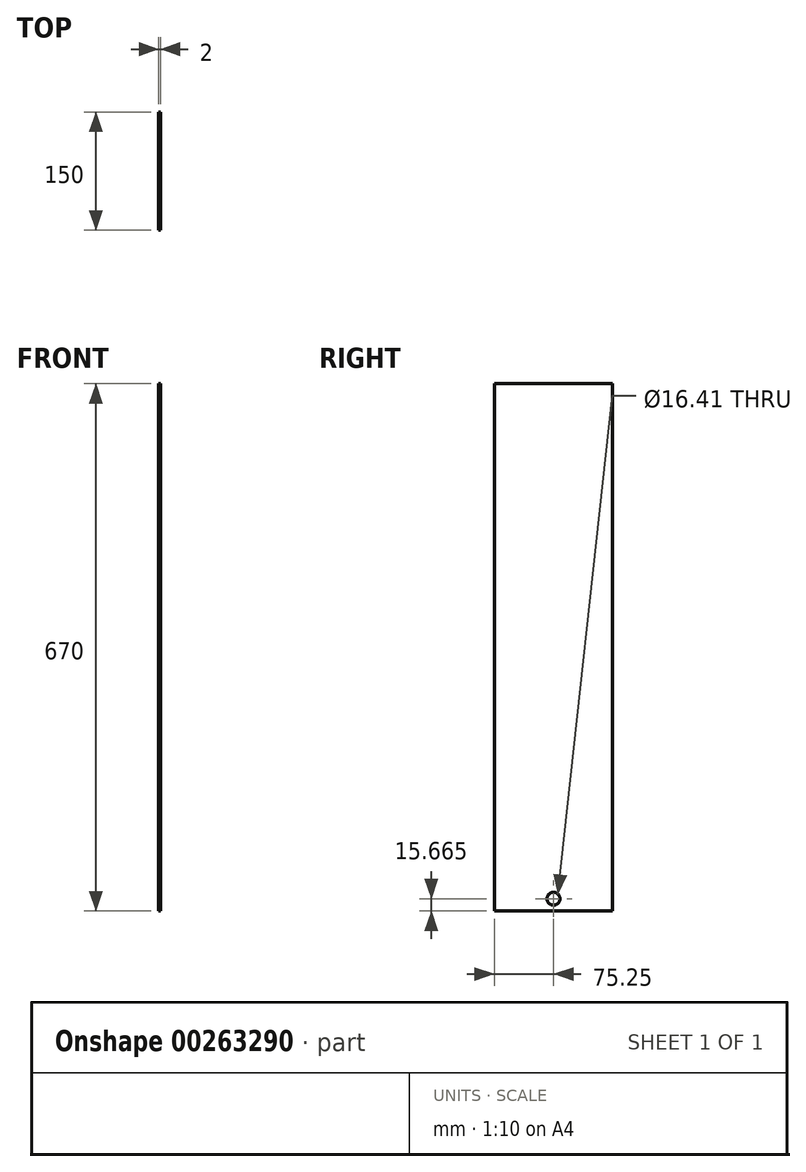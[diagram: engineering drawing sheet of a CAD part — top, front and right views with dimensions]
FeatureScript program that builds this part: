
annotation { "Feature Type Name" : "Feature", "Feature Type Description" : "" }
export const myFeature = defineFeature(function(context is Context, id is Id, definition is map)
    precondition{}
    {
        {
            var Q0;
            Q0=qCreatedBy(makeId("Right.planeOp"),FACE);
            var sketch = newSketch(context, id + "F0", { "sketchPlane" : qUnion([Q0])});
            skLineSegment(sketch, "E0.bottom", {"start": v(-80.14, -335) * mm, "end": v(69.86, -335) * mm});
            skLineSegment(sketch, "E0.top", {"start": v(-80.14, 335) * mm, "end": v(69.86, 335) * mm});
            skLineSegment(sketch, "E0.left", {"start": v(-80.14, -335) * mm, "end": v(-80.14, 335) * mm});
            skLineSegment(sketch, "E0.right", {"start": v(69.86, -335) * mm, "end": v(69.86, 335) * mm});
            skPoint(sketch, "E0.middle", {"position": v(-5.14, 0) * mm});
            skSolve(sketch);
        }
        {
            var Q0;
            Q0 = qSketchRegion(id + "F0", true);
            extrude(context, id + "F1", {"entities" : qUnion([Q0]), "depth" : 2 * mm});
        }
        {
            var Q0;
            Q0=makeQuery(id+"F1.opExtrude","CAP_FACE",FACE,{"disambiguationData":[OSD([sQuery(id+"F0.wireOp",EDGE,"E0.bottom"),sQuery(id+"F0.wireOp",EDGE,"E0.top"),sQuery(id+"F0.wireOp",EDGE,"E0.left"),sQuery(id+"F0.wireOp",EDGE,"E0.right")])],"isStart":true});
            var sketch = newSketch(context, id + "F2", { "sketchPlane" : qUnion([Q0])});
            skCircle(sketch, "E1", {"center": v(4.9, -319.33) * mm, "radius": 8.2 * mm});
            skSolve(sketch);
        }
        {
            var Q0;
            Q0 = qSketchRegion(id + "F2", true);
            extrude(context, id + "F3", {"entities" : qUnion([Q0]), "operationType" : NewBodyOperationType.REMOVE, "oppositeDirection" : true, "depth" : 25 * mm});
        }
    });
